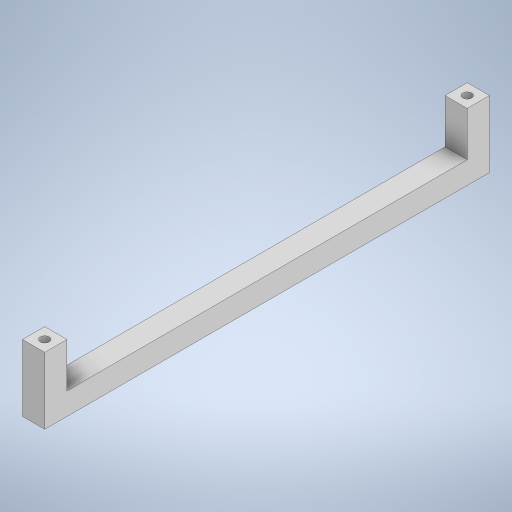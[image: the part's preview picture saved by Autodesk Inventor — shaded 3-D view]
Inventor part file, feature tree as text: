
AUTODESK INVENTOR PART (.ipt)
format: ipt  version: 2023 (Build 270158000, 158)  size: 254,464 bytes
history: native  units: in
note: dims shown in document units (in); Inventor stores cm internally (conversion verified against a paired STEP export)
features: extrude x3, sketch x3
ambient origin geometry x8: Origin, YZ Plane, XZ Plane, XY Plane, X Axis, Y Axis, Z Axis, Center Point
bodies: Solid1 (feature_tree)
feature tree (6):
  extrude  "Extrusion1"  Depth=0.5in
  extrude  "Extrusion2"  Depth=0.5in
  extrude  "Extrusion3"  Depth=0.5in
  sketch  "Sketch1"  dims[d0=10.0in d1=0.5in]
  sketch  "Sketch2"  dims[d2=0.5in d3=0.0in d4=0.5in]
  sketch  "Sketch3"  dims[d5=1.0in d6=0.0in d7=0.197in d8=0.25in d9=0.25in d10=0.7874in d12=9.5in d13=0.3937in d15=1.0in d17=1.0in d18=0.0in d19=0.5in d20=0.0344in]
